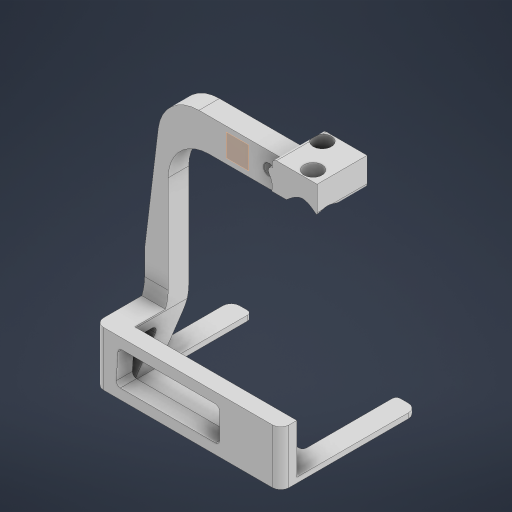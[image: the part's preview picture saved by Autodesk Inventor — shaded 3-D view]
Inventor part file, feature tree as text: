
AUTODESK INVENTOR PART (.ipt)
format: ipt  version: 2024.2 (Build 282272000, 272)  size: 343,040 bytes
history: native  units: in
note: dims shown in document units (in); Inventor stores cm internally (conversion verified against a paired STEP export)
features: other x3, sketch x1, plane x1
ambient origin geometry x8: Origin, YZ Plane, XZ Plane, XY Plane, X Axis, Y Axis, Z Axis, Center Point
bodies: Solid1 (feature_tree)
feature tree (5):
  other  "Leg.ipt"
  other  "Solid1::Leg.ipt"
  other  "TaggingFeature1"
  sketch  "Sketch3"  dims[d0=0.3937in]
  plane  "Work Plane1"
